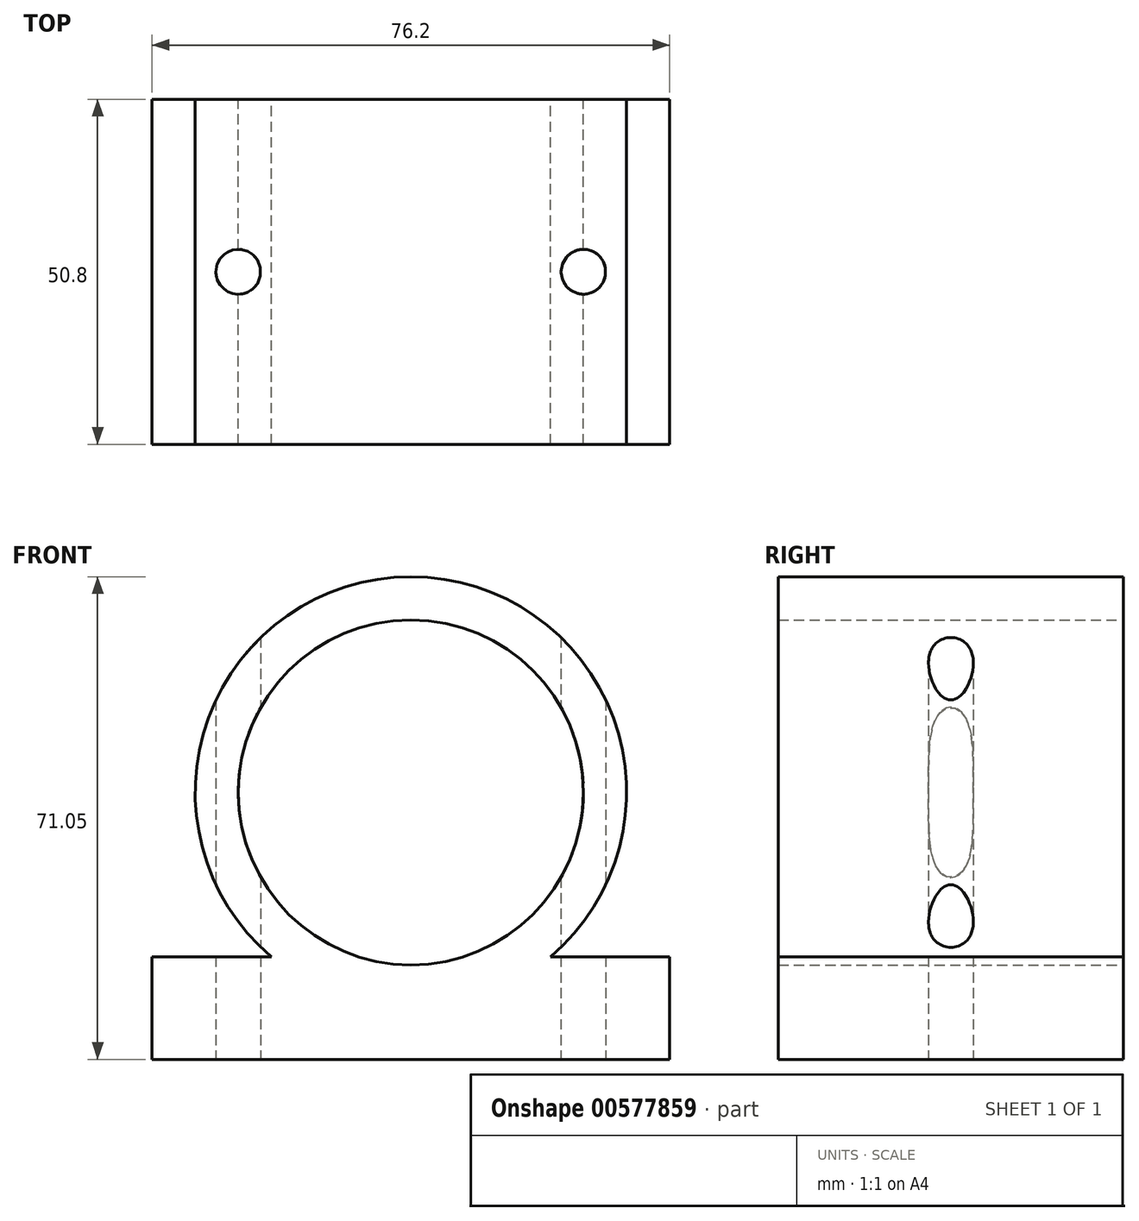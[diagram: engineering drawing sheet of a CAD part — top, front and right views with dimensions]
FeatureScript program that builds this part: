
annotation { "Feature Type Name" : "Feature", "Feature Type Description" : "" }
export const myFeature = defineFeature(function(context is Context, id is Id, definition is map)
    precondition{}
    {
        {
            var Q0;
            Q0=qCreatedBy(makeId("Front.planeOp"),FACE);
            var sketch = newSketch(context, id + "F0", { "sketchPlane" : qUnion([Q0])});
            skCircle(sketch, "E0", {"center": v(0, 0) * mm, "radius": 25.4 * mm});
            skCircle(sketch, "E1", {"center": v(0, 0) * mm, "radius": 31.75 * mm});
            skLineSegment(sketch, "E2.bottom", {"start": v(38.1, -39.3) * mm, "end": v(-38.1, -39.3) * mm});
            skLineSegment(sketch, "E2.top", {"start": v(38.1, -24.2) * mm, "end": v(-38.1, -24.2) * mm});
            skLineSegment(sketch, "E2.left", {"start": v(38.1, -39.3) * mm, "end": v(38.1, -24.2) * mm});
            skLineSegment(sketch, "E2.right", {"start": v(-38.1, -39.3) * mm, "end": v(-38.1, -24.2) * mm});
            skPoint(sketch, "E2.middle", {"position": v(0, -31.75) * mm});
            skSolve(sketch);
        }
        {
            var Q0;
            Q0 = qSketchRegion(id + "F0", true);
            extrude(context, id + "F1", {"entities" : qUnion([Q0]), "depth" : 50.8 * mm, "offsetDistance" : 25.4 * mm});
        }
        {
            var Q0;
            Q0=makeQuery(id+"F1.opExtrude","SWEPT_FACE",FACE,{"disambiguationData":[OSD([sQuery(id+"F0.wireOp",EDGE,"E2.bottom")])]});
            var sketch = newSketch(context, id + "F2", { "sketchPlane" : qUnion([Q0])});
            skLineSegment(sketch, "E3", {"start": v(-38.1, 25.4) * mm, "end": v(38.1, 25.4) * mm});
            skLineSegment(sketch, "E4", {"start": v(0, 50.8) * mm, "end": v(0, 0) * mm});
            skCircle(sketch, "E5", {"center": v(-25.4, 25.4) * mm, "radius": 3.3 * mm});
            skCircle(sketch, "E6.MirrorC", {"center": v(25.4, 25.4) * mm, "radius": 3.3 * mm});
            skSolve(sketch);
        }
        {
            var Q0;
            Q0=sQuery(id+"F2.wireOp",VERTEX,"E5.center");
            var Q1;
            Q1=sQuery(id+"F2.wireOp",VERTEX,"E6.MirrorC.center");
            var Q2;
            Q2=makeQuery(id+"F1.opExtrude","SWEPT_BODY",BODY,{"disambiguationData":[OSD([sQuery(id+"F0.wireOp",EDGE,"E0"),sQuery(id+"F0.wireOp",EDGE,"E1"),sQuery(id+"F0.wireOp",EDGE,"E2.bottom"),sQuery(id+"F0.wireOp",EDGE,"E2.top"),sQuery(id+"F0.wireOp",EDGE,"E2.left"),sQuery(id+"F0.wireOp",EDGE,"E2.right")])]});
            hole(context, id + "F3", {"style" : HoleStyle.SIMPLE, "endStyle" : HoleEndStyle.THROUGH, "holeDiameter" : 6.6 * mm, "isTappedThrough" : true, "tappedDepth" : 12.7 * mm, "tapClearance" : 3, "locations" : qUnion([Q0, Q1]), "scope" : qUnion([Q2])});
        }
    });
